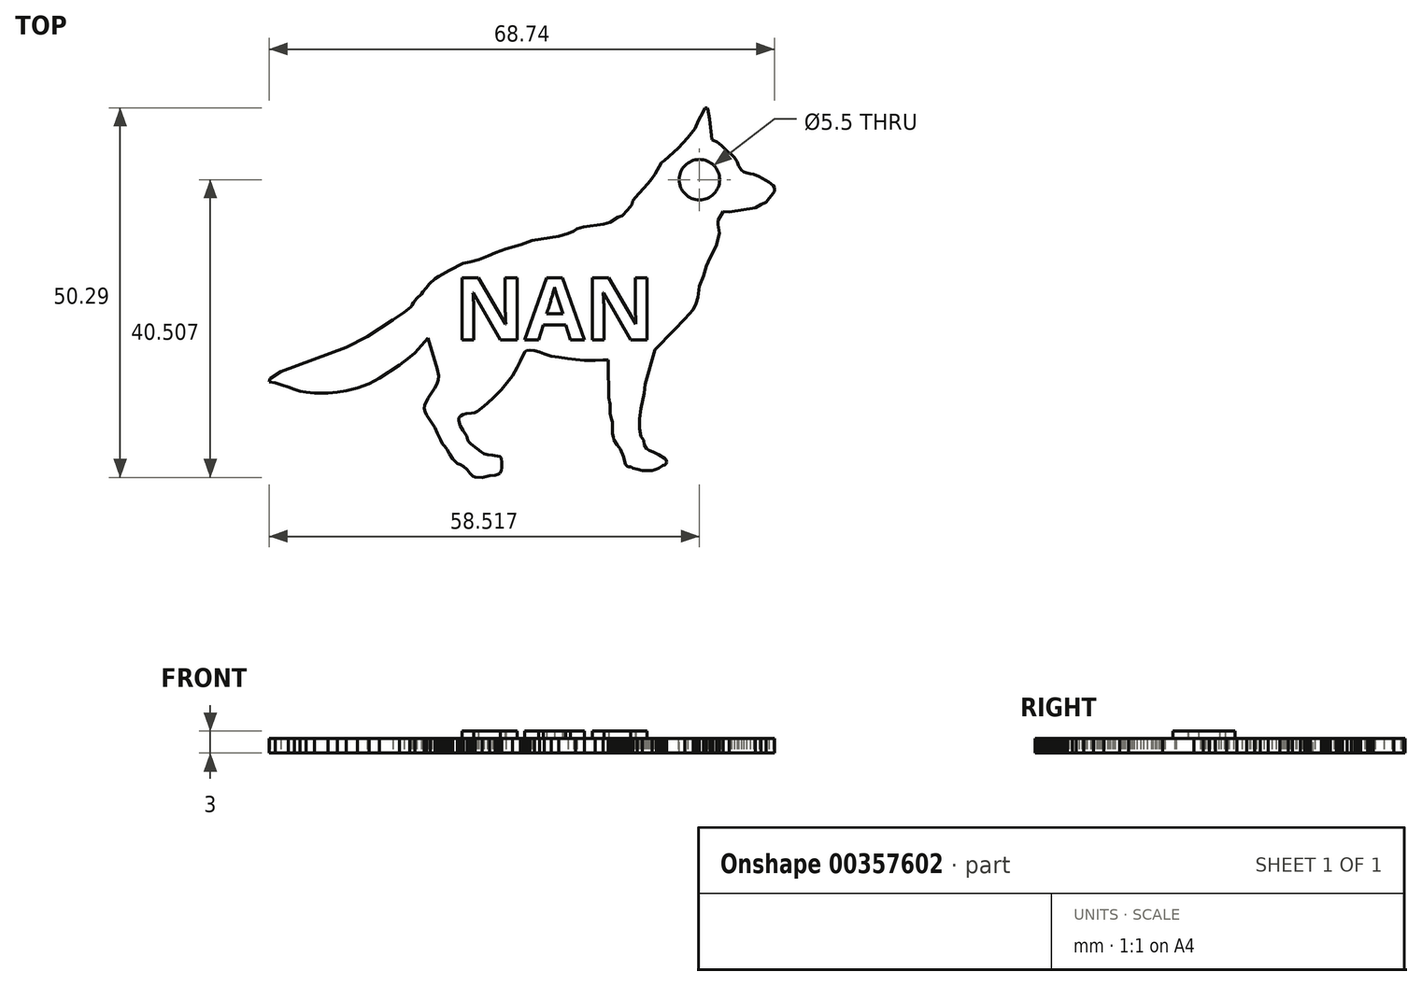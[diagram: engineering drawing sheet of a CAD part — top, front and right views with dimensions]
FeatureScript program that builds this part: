
annotation { "Feature Type Name" : "Feature", "Feature Type Description" : "" }
export const myFeature = defineFeature(function(context is Context, id is Id, definition is map)
    precondition{}
    {
        {
            var Q0;
            Q0=qCreatedBy(makeId("Top.planeOp"),FACE);
            var sketch = newSketch(context, id + "F0", { "sketchPlane" : qUnion([Q0])});
            skLineSegment(sketch, "E0", {"start": v(-14.95, 2.9) * mm, "end": v(-15.77, 3.38) * mm});
            skLineSegment(sketch, "E1", {"start": v(-15.77, 3.38) * mm, "end": v(-16.53, 3.78) * mm});
            skLineSegment(sketch, "E2", {"start": v(-16.53, 3.78) * mm, "end": v(-17.02, 3.97) * mm});
            skLineSegment(sketch, "E3", {"start": v(-17.02, 3.97) * mm, "end": v(-17.43, 4.22) * mm});
            skLineSegment(sketch, "E4", {"start": v(-17.43, 4.22) * mm, "end": v(-17.7, 4.7) * mm});
            skLineSegment(sketch, "E5", {"start": v(-17.7, 4.7) * mm, "end": v(-17.81, 5.35) * mm});
            skLineSegment(sketch, "E6", {"start": v(-17.81, 5.35) * mm, "end": v(-18.15, 5.86) * mm});
            skLineSegment(sketch, "E7", {"start": v(-18.15, 5.86) * mm, "end": v(-18.38, 6.92) * mm});
            skLineSegment(sketch, "E8", {"start": v(-18.38, 6.92) * mm, "end": v(-18.38, 8.25) * mm});
            skLineSegment(sketch, "E9", {"start": v(-18.38, 8.25) * mm, "end": v(-18.15, 9.65) * mm});
            skLineSegment(sketch, "E10", {"start": v(-18.15, 9.65) * mm, "end": v(-17.73, 11.8) * mm});
            skLineSegment(sketch, "E11", {"start": v(-17.73, 11.8) * mm, "end": v(-17.59, 12.98) * mm});
            skLineSegment(sketch, "E12", {"start": v(-17.59, 12.98) * mm, "end": v(-16.27, 17.65) * mm});
            skLineSegment(sketch, "E13", {"start": v(-16.27, 17.65) * mm, "end": v(-13.66, 20.33) * mm});
            skLineSegment(sketch, "E14", {"start": v(-13.66, 20.33) * mm, "end": v(-12.2, 21.87) * mm});
            skLineSegment(sketch, "E15", {"start": v(-12.2, 21.87) * mm, "end": v(-11.03, 23.13) * mm});
            skLineSegment(sketch, "E16", {"start": v(-11.03, 23.13) * mm, "end": v(-10.68, 23.98) * mm});
            skLineSegment(sketch, "E17", {"start": v(-10.68, 23.98) * mm, "end": v(-10.4, 24.8) * mm});
            skLineSegment(sketch, "E18", {"start": v(-10.4, 24.8) * mm, "end": v(-10.22, 26.33) * mm});
            skLineSegment(sketch, "E19", {"start": v(-10.22, 26.33) * mm, "end": v(-9.66, 27.72) * mm});
            skLineSegment(sketch, "E20", {"start": v(-9.66, 27.72) * mm, "end": v(-9.26, 29.04) * mm});
            skLineSegment(sketch, "E21", {"start": v(-9.26, 29.04) * mm, "end": v(-8.8, 30.16) * mm});
            skLineSegment(sketch, "E22", {"start": v(-8.8, 30.16) * mm, "end": v(-8.37, 30.9) * mm});
            skLineSegment(sketch, "E23", {"start": v(-8.37, 30.9) * mm, "end": v(-7.9, 31.98) * mm});
            skLineSegment(sketch, "E24", {"start": v(-7.9, 31.98) * mm, "end": v(-7.53, 33.57) * mm});
            skLineSegment(sketch, "E25", {"start": v(-7.53, 33.57) * mm, "end": v(-7.7, 34.7) * mm});
            skLineSegment(sketch, "E26", {"start": v(-7.7, 34.7) * mm, "end": v(-7.7, 35.26) * mm});
            skLineSegment(sketch, "E27", {"start": v(-7.7, 35.26) * mm, "end": v(-7, 36.5) * mm});
            skLineSegment(sketch, "E28", {"start": v(-7, 36.5) * mm, "end": v(-6.16, 36.4) * mm});
            skLineSegment(sketch, "E29", {"start": v(-6.16, 36.4) * mm, "end": v(-4.4, 36.68) * mm});
            skLineSegment(sketch, "E30", {"start": v(-4.4, 36.68) * mm, "end": v(-2.64, 36.96) * mm});
            skLineSegment(sketch, "E31", {"start": v(-2.64, 36.96) * mm, "end": v(-1.86, 37.41) * mm});
            skLineSegment(sketch, "E32", {"start": v(-1.86, 37.41) * mm, "end": v(-1.15, 37.72) * mm});
            skLineSegment(sketch, "E33", {"start": v(-1.15, 37.72) * mm, "end": v(0, 39.23) * mm});
            skLineSegment(sketch, "E34", {"start": v(0, 39.23) * mm, "end": v(0, 39.7) * mm});
            skLineSegment(sketch, "E35", {"start": v(0, 39.7) * mm, "end": v(-0.19, 40.04) * mm});
            skLineSegment(sketch, "E36", {"start": v(-0.19, 40.04) * mm, "end": v(-0.76, 40.45) * mm});
            skLineSegment(sketch, "E37", {"start": v(-0.76, 40.45) * mm, "end": v(-1.46, 40.85) * mm});
            skLineSegment(sketch, "E38", {"start": v(-1.46, 40.85) * mm, "end": v(-2.12, 41.23) * mm});
            skLineSegment(sketch, "E39", {"start": v(-2.12, 41.23) * mm, "end": v(-2.87, 41.52) * mm});
            skLineSegment(sketch, "E40", {"start": v(-2.87, 41.52) * mm, "end": v(-3.3, 41.64) * mm});
            skLineSegment(sketch, "E41", {"start": v(-3.3, 41.64) * mm, "end": v(-3.84, 41.73) * mm});
            skLineSegment(sketch, "E42", {"start": v(-3.84, 41.73) * mm, "end": v(-4.2, 41.84) * mm});
            skLineSegment(sketch, "E43", {"start": v(-4.2, 41.84) * mm, "end": v(-4.5, 42.1) * mm});
            skLineSegment(sketch, "E44", {"start": v(-4.5, 42.1) * mm, "end": v(-4.9, 42.72) * mm});
            skLineSegment(sketch, "E45", {"start": v(-4.9, 42.72) * mm, "end": v(-5.1, 43.29) * mm});
            skLineSegment(sketch, "E46", {"start": v(-5.1, 43.29) * mm, "end": v(-5.45, 43.82) * mm});
            skLineSegment(sketch, "E47", {"start": v(-5.45, 43.82) * mm, "end": v(-5.85, 44.2) * mm});
            skLineSegment(sketch, "E48", {"start": v(-5.85, 44.2) * mm, "end": v(-6.3, 44.53) * mm});
            skLineSegment(sketch, "E49", {"start": v(-6.3, 44.53) * mm, "end": v(-6.68, 44.91) * mm});
            skLineSegment(sketch, "E50", {"start": v(-6.68, 44.91) * mm, "end": v(-7.25, 45.5) * mm});
            skLineSegment(sketch, "E51", {"start": v(-7.25, 45.5) * mm, "end": v(-7.83, 45.96) * mm});
            skLineSegment(sketch, "E52", {"start": v(-7.83, 45.96) * mm, "end": v(-8.37, 46.17) * mm});
            skLineSegment(sketch, "E53", {"start": v(-8.37, 46.17) * mm, "end": v(-8.54, 46.27) * mm});
            skLineSegment(sketch, "E54", {"start": v(-8.54, 46.27) * mm, "end": v(-8.7, 47.7) * mm});
            skLineSegment(sketch, "E55", {"start": v(-8.7, 47.7) * mm, "end": v(-8.85, 49.08) * mm});
            skLineSegment(sketch, "E56", {"start": v(-8.85, 49.08) * mm, "end": v(-8.98, 49.9) * mm});
            skLineSegment(sketch, "E57", {"start": v(-8.98, 49.9) * mm, "end": v(-9.07, 50.42) * mm});
            skLineSegment(sketch, "E58", {"start": v(-9.07, 50.42) * mm, "end": v(-9.18, 50.6) * mm});
            skLineSegment(sketch, "E59", {"start": v(-9.18, 50.6) * mm, "end": v(-9.49, 50.6) * mm});
            skLineSegment(sketch, "E60", {"start": v(-9.49, 50.6) * mm, "end": v(-9.72, 50) * mm});
            skLineSegment(sketch, "E61", {"start": v(-9.72, 50) * mm, "end": v(-10.4, 48.84) * mm});
            skLineSegment(sketch, "E62", {"start": v(-10.4, 48.84) * mm, "end": v(-10.82, 47.75) * mm});
            skLineSegment(sketch, "E63", {"start": v(-10.82, 47.75) * mm, "end": v(-11.83, 46.54) * mm});
            skLineSegment(sketch, "E64", {"start": v(-11.83, 46.54) * mm, "end": v(-13.12, 45.13) * mm});
            skLineSegment(sketch, "E65", {"start": v(-13.12, 45.13) * mm, "end": v(-14.32, 44.02) * mm});
            skLineSegment(sketch, "E66", {"start": v(-14.32, 44.02) * mm, "end": v(-14.98, 43.42) * mm});
            skLineSegment(sketch, "E67", {"start": v(-14.98, 43.42) * mm, "end": v(-15.37, 43.16) * mm});
            skLineSegment(sketch, "E68", {"start": v(-15.37, 43.16) * mm, "end": v(-15.71, 42.57) * mm});
            skLineSegment(sketch, "E69", {"start": v(-15.71, 42.57) * mm, "end": v(-16, 42.06) * mm});
            skLineSegment(sketch, "E70", {"start": v(-16, 42.06) * mm, "end": v(-16.28, 41.58) * mm});
            skLineSegment(sketch, "E71", {"start": v(-16.28, 41.58) * mm, "end": v(-16.73, 40.92) * mm});
            skLineSegment(sketch, "E72", {"start": v(-16.73, 40.92) * mm, "end": v(-17.23, 40.3) * mm});
            skLineSegment(sketch, "E73", {"start": v(-17.23, 40.3) * mm, "end": v(-17.66, 39.84) * mm});
            skLineSegment(sketch, "E74", {"start": v(-17.66, 39.84) * mm, "end": v(-18.32, 39.12) * mm});
            skLineSegment(sketch, "E75", {"start": v(-18.32, 39.12) * mm, "end": v(-19.03, 38.34) * mm});
            skLineSegment(sketch, "E76", {"start": v(-19.03, 38.34) * mm, "end": v(-19.31, 37.85) * mm});
            skLineSegment(sketch, "E77", {"start": v(-19.31, 37.85) * mm, "end": v(-19.36, 37.43) * mm});
            skLineSegment(sketch, "E78", {"start": v(-19.36, 37.43) * mm, "end": v(-20, 36.64) * mm});
            skLineSegment(sketch, "E79", {"start": v(-20, 36.64) * mm, "end": v(-20.7, 35.88) * mm});
            skLineSegment(sketch, "E80", {"start": v(-20.7, 35.88) * mm, "end": v(-21.28, 35.72) * mm});
            skLineSegment(sketch, "E81", {"start": v(-21.28, 35.72) * mm, "end": v(-21.99, 35.26) * mm});
            skLineSegment(sketch, "E82", {"start": v(-21.99, 35.26) * mm, "end": v(-22.36, 35.02) * mm});
            skLineSegment(sketch, "E83", {"start": v(-22.36, 35.02) * mm, "end": v(-23.28, 34.77) * mm});
            skLineSegment(sketch, "E84", {"start": v(-23.28, 34.77) * mm, "end": v(-24.64, 34.56) * mm});
            skLineSegment(sketch, "E85", {"start": v(-24.64, 34.56) * mm, "end": v(-25.96, 34.35) * mm});
            skLineSegment(sketch, "E86", {"start": v(-25.96, 34.35) * mm, "end": v(-26.87, 34.1) * mm});
            skLineSegment(sketch, "E87", {"start": v(-26.87, 34.1) * mm, "end": v(-27.33, 33.8) * mm});
            skLineSegment(sketch, "E88", {"start": v(-27.33, 33.8) * mm, "end": v(-28.05, 33.46) * mm});
            skLineSegment(sketch, "E89", {"start": v(-28.05, 33.46) * mm, "end": v(-29.37, 33.1) * mm});
            skLineSegment(sketch, "E90", {"start": v(-29.37, 33.1) * mm, "end": v(-33, 32.52) * mm});
            skLineSegment(sketch, "E91", {"start": v(-33, 32.52) * mm, "end": v(-34.5, 31.95) * mm});
            skLineSegment(sketch, "E92", {"start": v(-34.5, 31.95) * mm, "end": v(-35.33, 31.72) * mm});
            skLineSegment(sketch, "E93", {"start": v(-35.33, 31.72) * mm, "end": v(-36.54, 31.39) * mm});
            skLineSegment(sketch, "E94", {"start": v(-36.54, 31.39) * mm, "end": v(-37.9, 30.86) * mm});
            skLineSegment(sketch, "E95", {"start": v(-37.9, 30.86) * mm, "end": v(-38.91, 30.41) * mm});
            skLineSegment(sketch, "E96", {"start": v(-38.91, 30.41) * mm, "end": v(-40.2, 29.93) * mm});
            skLineSegment(sketch, "E97", {"start": v(-40.2, 29.93) * mm, "end": v(-41.45, 29.6) * mm});
            skLineSegment(sketch, "E98", {"start": v(-41.45, 29.6) * mm, "end": v(-42.34, 29.45) * mm});
            skLineSegment(sketch, "E99", {"start": v(-42.34, 29.45) * mm, "end": v(-44.21, 28.45) * mm});
            skLineSegment(sketch, "E100", {"start": v(-44.21, 28.45) * mm, "end": v(-45.68, 27.64) * mm});
            skLineSegment(sketch, "E101", {"start": v(-45.68, 27.64) * mm, "end": v(-46.17, 27.32) * mm});
            skLineSegment(sketch, "E102", {"start": v(-46.17, 27.32) * mm, "end": v(-46.92, 26.63) * mm});
            skLineSegment(sketch, "E103", {"start": v(-46.92, 26.63) * mm, "end": v(-47.4, 26.04) * mm});
            skLineSegment(sketch, "E104", {"start": v(-47.4, 26.04) * mm, "end": v(-47.83, 25.56) * mm});
            skLineSegment(sketch, "E105", {"start": v(-47.83, 25.56) * mm, "end": v(-48, 25.25) * mm});
            skLineSegment(sketch, "E106", {"start": v(-48, 25.25) * mm, "end": v(-48.68, 24.63) * mm});
            skLineSegment(sketch, "E107", {"start": v(-48.68, 24.63) * mm, "end": v(-49.1, 24.1) * mm});
            skLineSegment(sketch, "E108", {"start": v(-49.1, 24.1) * mm, "end": v(-49.3, 23.77) * mm});
            skLineSegment(sketch, "E109", {"start": v(-49.3, 23.77) * mm, "end": v(-49.4, 23.49) * mm});
            skLineSegment(sketch, "E110", {"start": v(-49.4, 23.49) * mm, "end": v(-50.38, 22.77) * mm});
            skLineSegment(sketch, "E111", {"start": v(-50.38, 22.77) * mm, "end": v(-51.87, 21.74) * mm});
            skLineSegment(sketch, "E112", {"start": v(-51.87, 21.74) * mm, "end": v(-53.68, 20.56) * mm});
            skLineSegment(sketch, "E113", {"start": v(-53.68, 20.56) * mm, "end": v(-55.36, 19.48) * mm});
            skLineSegment(sketch, "E114", {"start": v(-55.36, 19.48) * mm, "end": v(-58.23, 17.97) * mm});
            skLineSegment(sketch, "E115", {"start": v(-58.23, 17.97) * mm, "end": v(-61, 16.94) * mm});
            skLineSegment(sketch, "E116", {"start": v(-61, 16.94) * mm, "end": v(-63.15, 16.14) * mm});
            skLineSegment(sketch, "E117", {"start": v(-63.15, 16.14) * mm, "end": v(-65.63, 15.22) * mm});
            skLineSegment(sketch, "E118", {"start": v(-65.63, 15.22) * mm, "end": v(-67.14, 14.66) * mm});
            skLineSegment(sketch, "E119", {"start": v(-67.14, 14.66) * mm, "end": v(-68, 14.1) * mm});
            skLineSegment(sketch, "E120", {"start": v(-68, 14.1) * mm, "end": v(-68.58, 13.73) * mm});
            skLineSegment(sketch, "E121", {"start": v(-68.58, 13.73) * mm, "end": v(-68.74, 13.32) * mm});
            skLineSegment(sketch, "E122", {"start": v(-68.74, 13.32) * mm, "end": v(-67.9, 13.15) * mm});
            skLineSegment(sketch, "E123", {"start": v(-67.9, 13.15) * mm, "end": v(-66.97, 12.84) * mm});
            skLineSegment(sketch, "E124", {"start": v(-66.97, 12.84) * mm, "end": v(-66.14, 12.58) * mm});
            skLineSegment(sketch, "E125", {"start": v(-66.14, 12.58) * mm, "end": v(-65.31, 12.25) * mm});
            skLineSegment(sketch, "E126", {"start": v(-65.31, 12.25) * mm, "end": v(-64.52, 12.02) * mm});
            skLineSegment(sketch, "E127", {"start": v(-64.52, 12.02) * mm, "end": v(-63.68, 11.92) * mm});
            skLineSegment(sketch, "E128", {"start": v(-63.68, 11.92) * mm, "end": v(-62.6, 11.8) * mm});
            skLineSegment(sketch, "E129", {"start": v(-62.6, 11.8) * mm, "end": v(-60.73, 11.8) * mm});
            skLineSegment(sketch, "E130", {"start": v(-60.73, 11.8) * mm, "end": v(-59.44, 11.88) * mm});
            skLineSegment(sketch, "E131", {"start": v(-59.44, 11.88) * mm, "end": v(-58.22, 12.07) * mm});
            skLineSegment(sketch, "E132", {"start": v(-58.22, 12.07) * mm, "end": v(-56.72, 12.48) * mm});
            skLineSegment(sketch, "E133", {"start": v(-56.72, 12.48) * mm, "end": v(-55.15, 13.06) * mm});
            skLineSegment(sketch, "E134", {"start": v(-55.15, 13.06) * mm, "end": v(-53.74, 13.78) * mm});
            skLineSegment(sketch, "E135", {"start": v(-53.74, 13.78) * mm, "end": v(-52.55, 14.56) * mm});
            skLineSegment(sketch, "E136", {"start": v(-52.55, 14.56) * mm, "end": v(-51, 15.56) * mm});
            skLineSegment(sketch, "E137", {"start": v(-51, 15.56) * mm, "end": v(-49.58, 16.64) * mm});
            skLineSegment(sketch, "E138", {"start": v(-49.58, 16.64) * mm, "end": v(-48.94, 17.2) * mm});
            skLineSegment(sketch, "E139", {"start": v(-48.94, 17.2) * mm, "end": v(-47.13, 19.27) * mm});
            skLineSegment(sketch, "E140", {"start": v(-47.13, 19.27) * mm, "end": v(-46.18, 16.12) * mm});
            skLineSegment(sketch, "E141", {"start": v(-46.18, 16.12) * mm, "end": v(-45.84, 15.01) * mm});
            skLineSegment(sketch, "E142", {"start": v(-45.84, 15.01) * mm, "end": v(-45.69, 14.15) * mm});
            skLineSegment(sketch, "E143", {"start": v(-45.69, 14.15) * mm, "end": v(-45.73, 13.58) * mm});
            skLineSegment(sketch, "E144", {"start": v(-45.73, 13.58) * mm, "end": v(-45.9, 12.97) * mm});
            skLineSegment(sketch, "E145", {"start": v(-45.9, 12.97) * mm, "end": v(-46.23, 12.4) * mm});
            skLineSegment(sketch, "E146", {"start": v(-46.23, 12.4) * mm, "end": v(-46.63, 11.84) * mm});
            skLineSegment(sketch, "E147", {"start": v(-46.63, 11.84) * mm, "end": v(-47.15, 11.08) * mm});
            skLineSegment(sketch, "E148", {"start": v(-47.15, 11.08) * mm, "end": v(-47.6, 10.14) * mm});
            skLineSegment(sketch, "E149", {"start": v(-47.6, 10.14) * mm, "end": v(-47.63, 9.65) * mm});
            skLineSegment(sketch, "E150", {"start": v(-47.63, 9.65) * mm, "end": v(-47.54, 9.2) * mm});
            skLineSegment(sketch, "E151", {"start": v(-47.54, 9.2) * mm, "end": v(-47.33, 8.8) * mm});
            skLineSegment(sketch, "E152", {"start": v(-47.33, 8.8) * mm, "end": v(-46.82, 8.01) * mm});
            skLineSegment(sketch, "E153", {"start": v(-46.82, 8.01) * mm, "end": v(-46.18, 7.06) * mm});
            skLineSegment(sketch, "E154", {"start": v(-46.18, 7.06) * mm, "end": v(-45.86, 6.3) * mm});
            skLineSegment(sketch, "E155", {"start": v(-45.86, 6.3) * mm, "end": v(-45.43, 5.45) * mm});
            skLineSegment(sketch, "E156", {"start": v(-45.43, 5.45) * mm, "end": v(-45.16, 4.88) * mm});
            skLineSegment(sketch, "E157", {"start": v(-45.16, 4.88) * mm, "end": v(-44.86, 4.52) * mm});
            skLineSegment(sketch, "E158", {"start": v(-44.86, 4.52) * mm, "end": v(-44.53, 4.06) * mm});
            skLineSegment(sketch, "E159", {"start": v(-44.53, 4.06) * mm, "end": v(-44.2, 3.5) * mm});
            skLineSegment(sketch, "E160", {"start": v(-44.2, 3.5) * mm, "end": v(-43.76, 2.83) * mm});
            skLineSegment(sketch, "E161", {"start": v(-43.76, 2.83) * mm, "end": v(-43.14, 2.17) * mm});
            skLineSegment(sketch, "E162", {"start": v(-43.14, 2.17) * mm, "end": v(-42.73, 2.09) * mm});
            skLineSegment(sketch, "E163", {"start": v(-42.73, 2.09) * mm, "end": v(-42.3, 1.8) * mm});
            skLineSegment(sketch, "E164", {"start": v(-42.3, 1.8) * mm, "end": v(-41.8, 1.37) * mm});
            skLineSegment(sketch, "E165", {"start": v(-41.8, 1.37) * mm, "end": v(-41.44, 0.88) * mm});
            skLineSegment(sketch, "E166", {"start": v(-41.44, 0.88) * mm, "end": v(-41.02, 0.5) * mm});
            skLineSegment(sketch, "E167", {"start": v(-41.02, 0.5) * mm, "end": v(-40.75, 0.35) * mm});
            skLineSegment(sketch, "E168", {"start": v(-40.75, 0.35) * mm, "end": v(-39.74, 0.3) * mm});
            skLineSegment(sketch, "E169", {"start": v(-39.74, 0.3) * mm, "end": v(-38.76, 0.5) * mm});
            skLineSegment(sketch, "E170", {"start": v(-38.76, 0.5) * mm, "end": v(-37.96, 0.6) * mm});
            skLineSegment(sketch, "E171", {"start": v(-37.96, 0.6) * mm, "end": v(-37.63, 0.7) * mm});
            skLineSegment(sketch, "E172", {"start": v(-37.63, 0.7) * mm, "end": v(-37.35, 0.87) * mm});
            skLineSegment(sketch, "E173", {"start": v(-37.35, 0.87) * mm, "end": v(-37.16, 1.2) * mm});
            skLineSegment(sketch, "E174", {"start": v(-37.16, 1.2) * mm, "end": v(-37.08, 1.6) * mm});
            skLineSegment(sketch, "E175", {"start": v(-37.08, 1.6) * mm, "end": v(-37.08, 2.3) * mm});
            skLineSegment(sketch, "E176", {"start": v(-37.08, 2.3) * mm, "end": v(-37.17, 2.95) * mm});
            skLineSegment(sketch, "E177", {"start": v(-37.17, 2.95) * mm, "end": v(-37.34, 3.14) * mm});
            skLineSegment(sketch, "E178", {"start": v(-37.34, 3.14) * mm, "end": v(-37.74, 3.22) * mm});
            skLineSegment(sketch, "E179", {"start": v(-37.74, 3.22) * mm, "end": v(-38.35, 3.35) * mm});
            skLineSegment(sketch, "E180", {"start": v(-38.35, 3.35) * mm, "end": v(-38.99, 3.4) * mm});
            skLineSegment(sketch, "E181", {"start": v(-38.99, 3.4) * mm, "end": v(-39.5, 3.5) * mm});
            skLineSegment(sketch, "E182", {"start": v(-39.5, 3.5) * mm, "end": v(-39.92, 3.76) * mm});
            skLineSegment(sketch, "E183", {"start": v(-39.92, 3.76) * mm, "end": v(-40.48, 4.21) * mm});
            skLineSegment(sketch, "E184", {"start": v(-40.48, 4.21) * mm, "end": v(-41.3, 4.84) * mm});
            skLineSegment(sketch, "E185", {"start": v(-41.3, 4.84) * mm, "end": v(-41.6, 5.17) * mm});
            skLineSegment(sketch, "E186", {"start": v(-41.6, 5.17) * mm, "end": v(-41.73, 5.45) * mm});
            skLineSegment(sketch, "E187", {"start": v(-41.73, 5.45) * mm, "end": v(-41.87, 5.93) * mm});
            skLineSegment(sketch, "E188", {"start": v(-41.87, 5.93) * mm, "end": v(-42.36, 6.68) * mm});
            skLineSegment(sketch, "E189", {"start": v(-42.36, 6.68) * mm, "end": v(-42.76, 7.34) * mm});
            skLineSegment(sketch, "E190", {"start": v(-42.76, 7.34) * mm, "end": v(-42.96, 8.01) * mm});
            skLineSegment(sketch, "E191", {"start": v(-42.96, 8.01) * mm, "end": v(-42.96, 8.38) * mm});
            skLineSegment(sketch, "E192", {"start": v(-42.96, 8.38) * mm, "end": v(-42.7, 8.65) * mm});
            skLineSegment(sketch, "E193", {"start": v(-42.7, 8.65) * mm, "end": v(-42.35, 8.86) * mm});
            skLineSegment(sketch, "E194", {"start": v(-42.35, 8.86) * mm, "end": v(-41.9, 8.96) * mm});
            skLineSegment(sketch, "E195", {"start": v(-41.9, 8.96) * mm, "end": v(-41.2, 9.02) * mm});
            skLineSegment(sketch, "E196", {"start": v(-41.2, 9.02) * mm, "end": v(-40.81, 9.1) * mm});
            skLineSegment(sketch, "E197", {"start": v(-40.81, 9.1) * mm, "end": v(-40.41, 9.27) * mm});
            skLineSegment(sketch, "E198", {"start": v(-40.41, 9.27) * mm, "end": v(-39.84, 9.76) * mm});
            skLineSegment(sketch, "E199", {"start": v(-39.84, 9.76) * mm, "end": v(-39.04, 10.4) * mm});
            skLineSegment(sketch, "E200", {"start": v(-39.04, 10.4) * mm, "end": v(-38.2, 11.17) * mm});
            skLineSegment(sketch, "E201", {"start": v(-38.2, 11.17) * mm, "end": v(-37.15, 12.2) * mm});
            skLineSegment(sketch, "E202", {"start": v(-37.15, 12.2) * mm, "end": v(-36.4, 13.15) * mm});
            skLineSegment(sketch, "E203", {"start": v(-36.4, 13.15) * mm, "end": v(-35.6, 14.15) * mm});
            skLineSegment(sketch, "E204", {"start": v(-35.6, 14.15) * mm, "end": v(-35, 15.28) * mm});
            skLineSegment(sketch, "E205", {"start": v(-35, 15.28) * mm, "end": v(-34.55, 16.12) * mm});
            skLineSegment(sketch, "E206", {"start": v(-34.55, 16.12) * mm, "end": v(-34.24, 16.82) * mm});
            skLineSegment(sketch, "E207", {"start": v(-34.24, 16.82) * mm, "end": v(-33.95, 17.43) * mm});
            skLineSegment(sketch, "E208", {"start": v(-33.95, 17.43) * mm, "end": v(-33.71, 17.52) * mm});
            skLineSegment(sketch, "E209", {"start": v(-33.71, 17.52) * mm, "end": v(-33.3, 17.59) * mm});
            skLineSegment(sketch, "E210", {"start": v(-33.3, 17.59) * mm, "end": v(-32.65, 17.53) * mm});
            skLineSegment(sketch, "E211", {"start": v(-32.65, 17.53) * mm, "end": v(-31.95, 17.39) * mm});
            skLineSegment(sketch, "E212", {"start": v(-31.95, 17.39) * mm, "end": v(-31.33, 17.1) * mm});
            skLineSegment(sketch, "E213", {"start": v(-31.33, 17.1) * mm, "end": v(-30.35, 16.81) * mm});
            skLineSegment(sketch, "E214", {"start": v(-30.35, 16.81) * mm, "end": v(-29.36, 16.64) * mm});
            skLineSegment(sketch, "E215", {"start": v(-29.36, 16.64) * mm, "end": v(-28.16, 16.48) * mm});
            skLineSegment(sketch, "E216", {"start": v(-28.16, 16.48) * mm, "end": v(-27.05, 16.33) * mm});
            skLineSegment(sketch, "E217", {"start": v(-27.05, 16.33) * mm, "end": v(-25.85, 16.22) * mm});
            skLineSegment(sketch, "E218", {"start": v(-25.85, 16.22) * mm, "end": v(-24.4, 16.22) * mm});
            skLineSegment(sketch, "E219", {"start": v(-24.4, 16.22) * mm, "end": v(-23.3, 16.25) * mm});
            skLineSegment(sketch, "E220", {"start": v(-23.3, 16.25) * mm, "end": v(-22.65, 16.25) * mm});
            skLineSegment(sketch, "E221", {"start": v(-22.65, 16.25) * mm, "end": v(-22.65, 14.95) * mm});
            skLineSegment(sketch, "E222", {"start": v(-22.65, 14.95) * mm, "end": v(-22.65, 13.65) * mm});
            skLineSegment(sketch, "E223", {"start": v(-22.65, 13.65) * mm, "end": v(-22.58, 13.3) * mm});
            skLineSegment(sketch, "E224", {"start": v(-22.58, 13.3) * mm, "end": v(-22.54, 11.17) * mm});
            skLineSegment(sketch, "E225", {"start": v(-22.54, 11.17) * mm, "end": v(-22.49, 10.87) * mm});
            skLineSegment(sketch, "E226", {"start": v(-22.49, 10.87) * mm, "end": v(-22.41, 10.52) * mm});
            skLineSegment(sketch, "E227", {"start": v(-22.41, 10.52) * mm, "end": v(-22.35, 10.3) * mm});
            skLineSegment(sketch, "E228", {"start": v(-22.35, 10.3) * mm, "end": v(-22.35, 8.98) * mm});
            skLineSegment(sketch, "E229", {"start": v(-22.35, 8.98) * mm, "end": v(-22.28, 8.66) * mm});
            skLineSegment(sketch, "E230", {"start": v(-22.28, 8.66) * mm, "end": v(-22.19, 8.22) * mm});
            skLineSegment(sketch, "E231", {"start": v(-22.19, 8.22) * mm, "end": v(-22.03, 7.85) * mm});
            skLineSegment(sketch, "E232", {"start": v(-22.03, 7.85) * mm, "end": v(-22.03, 6.25) * mm});
            skLineSegment(sketch, "E233", {"start": v(-22.03, 6.25) * mm, "end": v(-21.93, 5.8) * mm});
            skLineSegment(sketch, "E234", {"start": v(-21.93, 5.8) * mm, "end": v(-21.83, 5.45) * mm});
            skLineSegment(sketch, "E235", {"start": v(-21.83, 5.45) * mm, "end": v(-21.64, 5.13) * mm});
            skLineSegment(sketch, "E236", {"start": v(-21.64, 5.13) * mm, "end": v(-21.4, 4.75) * mm});
            skLineSegment(sketch, "E237", {"start": v(-21.4, 4.75) * mm, "end": v(-21.17, 4.39) * mm});
            skLineSegment(sketch, "E238", {"start": v(-21.17, 4.39) * mm, "end": v(-21, 4.16) * mm});
            skLineSegment(sketch, "E239", {"start": v(-21, 4.16) * mm, "end": v(-20.72, 3.5) * mm});
            skLineSegment(sketch, "E240", {"start": v(-20.72, 3.5) * mm, "end": v(-20.52, 3.04) * mm});
            skLineSegment(sketch, "E241", {"start": v(-20.52, 3.04) * mm, "end": v(-20.41, 2.5) * mm});
            skLineSegment(sketch, "E242", {"start": v(-20.41, 2.5) * mm, "end": v(-20.27, 2.04) * mm});
            skLineSegment(sketch, "E243", {"start": v(-20.27, 2.04) * mm, "end": v(-20.04, 1.82) * mm});
            skLineSegment(sketch, "E244", {"start": v(-20.04, 1.82) * mm, "end": v(-19.85, 1.74) * mm});
            skLineSegment(sketch, "E245", {"start": v(-19.85, 1.74) * mm, "end": v(-19.52, 1.71) * mm});
            skLineSegment(sketch, "E246", {"start": v(-19.52, 1.71) * mm, "end": v(-19.23, 1.56) * mm});
            skLineSegment(sketch, "E247", {"start": v(-19.23, 1.56) * mm, "end": v(-18.68, 1.4) * mm});
            skLineSegment(sketch, "E248", {"start": v(-18.68, 1.4) * mm, "end": v(-17.98, 1.25) * mm});
            skLineSegment(sketch, "E249", {"start": v(-17.98, 1.25) * mm, "end": v(-16.65, 1.25) * mm});
            skLineSegment(sketch, "E250", {"start": v(-16.65, 1.25) * mm, "end": v(-16.1, 1.42) * mm});
            skLineSegment(sketch, "E251", {"start": v(-16.1, 1.42) * mm, "end": v(-15.73, 1.57) * mm});
            skLineSegment(sketch, "E252", {"start": v(-15.73, 1.57) * mm, "end": v(-15.4, 1.77) * mm});
            skLineSegment(sketch, "E253", {"start": v(-15.4, 1.77) * mm, "end": v(-15.17, 1.95) * mm});
            skLineSegment(sketch, "E254", {"start": v(-15.17, 1.95) * mm, "end": v(-14.93, 2) * mm});
            skLineSegment(sketch, "E255", {"start": v(-14.93, 2) * mm, "end": v(-14.75, 2.2) * mm});
            skLineSegment(sketch, "E256", {"start": v(-14.75, 2.2) * mm, "end": v(-14.7, 2.4) * mm});
            skLineSegment(sketch, "E257", {"start": v(-14.7, 2.4) * mm, "end": v(-14.76, 2.66) * mm});
            skLineSegment(sketch, "E258", {"start": v(-14.76, 2.66) * mm, "end": v(-14.95, 2.9) * mm});
            skSolve(sketch);
        }
        {
            var Q0;
            Q0 = qSketchRegion(id + "F0", true);
            extrude(context, id + "F1", {"entities" : qUnion([Q0]), "depth" : 2 * mm});
        }
        {
            var Q0;
            Q0=makeQuery(id+"F1.opExtrude","CAP_FACE",FACE,{"disambiguationData":[OSD([sQuery(id+"F0.wireOp",EDGE,"E0"),sQuery(id+"F0.wireOp",EDGE,"E1"),sQuery(id+"F0.wireOp",EDGE,"E2"),sQuery(id+"F0.wireOp",EDGE,"E3"),sQuery(id+"F0.wireOp",EDGE,"E4"),sQuery(id+"F0.wireOp",EDGE,"E5"),sQuery(id+"F0.wireOp",EDGE,"E6"),sQuery(id+"F0.wireOp",EDGE,"E7"),sQuery(id+"F0.wireOp",EDGE,"E8"),sQuery(id+"F0.wireOp",EDGE,"E9"),sQuery(id+"F0.wireOp",EDGE,"E10"),sQuery(id+"F0.wireOp",EDGE,"E11"),sQuery(id+"F0.wireOp",EDGE,"E12"),sQuery(id+"F0.wireOp",EDGE,"E13"),sQuery(id+"F0.wireOp",EDGE,"E14"),sQuery(id+"F0.wireOp",EDGE,"E15"),sQuery(id+"F0.wireOp",EDGE,"E16"),sQuery(id+"F0.wireOp",EDGE,"E17"),sQuery(id+"F0.wireOp",EDGE,"E18"),sQuery(id+"F0.wireOp",EDGE,"E19"),sQuery(id+"F0.wireOp",EDGE,"E20"),sQuery(id+"F0.wireOp",EDGE,"E21"),sQuery(id+"F0.wireOp",EDGE,"E22"),sQuery(id+"F0.wireOp",EDGE,"E23"),sQuery(id+"F0.wireOp",EDGE,"E24"),sQuery(id+"F0.wireOp",EDGE,"E25"),sQuery(id+"F0.wireOp",EDGE,"E26"),sQuery(id+"F0.wireOp",EDGE,"E27"),sQuery(id+"F0.wireOp",EDGE,"E28"),sQuery(id+"F0.wireOp",EDGE,"E29"),sQuery(id+"F0.wireOp",EDGE,"E30"),sQuery(id+"F0.wireOp",EDGE,"E31"),sQuery(id+"F0.wireOp",EDGE,"E32"),sQuery(id+"F0.wireOp",EDGE,"E33"),sQuery(id+"F0.wireOp",EDGE,"E34"),sQuery(id+"F0.wireOp",EDGE,"E35"),sQuery(id+"F0.wireOp",EDGE,"E36"),sQuery(id+"F0.wireOp",EDGE,"E37"),sQuery(id+"F0.wireOp",EDGE,"E38"),sQuery(id+"F0.wireOp",EDGE,"E39"),sQuery(id+"F0.wireOp",EDGE,"E40"),sQuery(id+"F0.wireOp",EDGE,"E41"),sQuery(id+"F0.wireOp",EDGE,"E42"),sQuery(id+"F0.wireOp",EDGE,"E43"),sQuery(id+"F0.wireOp",EDGE,"E44"),sQuery(id+"F0.wireOp",EDGE,"E45"),sQuery(id+"F0.wireOp",EDGE,"E46"),sQuery(id+"F0.wireOp",EDGE,"E47"),sQuery(id+"F0.wireOp",EDGE,"E48"),sQuery(id+"F0.wireOp",EDGE,"E49"),sQuery(id+"F0.wireOp",EDGE,"E50"),sQuery(id+"F0.wireOp",EDGE,"E51"),sQuery(id+"F0.wireOp",EDGE,"E52"),sQuery(id+"F0.wireOp",EDGE,"E53"),sQuery(id+"F0.wireOp",EDGE,"E54"),sQuery(id+"F0.wireOp",EDGE,"E55"),sQuery(id+"F0.wireOp",EDGE,"E56"),sQuery(id+"F0.wireOp",EDGE,"E57"),sQuery(id+"F0.wireOp",EDGE,"E58"),sQuery(id+"F0.wireOp",EDGE,"E59"),sQuery(id+"F0.wireOp",EDGE,"E60"),sQuery(id+"F0.wireOp",EDGE,"E61"),sQuery(id+"F0.wireOp",EDGE,"E62"),sQuery(id+"F0.wireOp",EDGE,"E63"),sQuery(id+"F0.wireOp",EDGE,"E64"),sQuery(id+"F0.wireOp",EDGE,"E65"),sQuery(id+"F0.wireOp",EDGE,"E66"),sQuery(id+"F0.wireOp",EDGE,"E67"),sQuery(id+"F0.wireOp",EDGE,"E68"),sQuery(id+"F0.wireOp",EDGE,"E69"),sQuery(id+"F0.wireOp",EDGE,"E70"),sQuery(id+"F0.wireOp",EDGE,"E71"),sQuery(id+"F0.wireOp",EDGE,"E72"),sQuery(id+"F0.wireOp",EDGE,"E73"),sQuery(id+"F0.wireOp",EDGE,"E74"),sQuery(id+"F0.wireOp",EDGE,"E75"),sQuery(id+"F0.wireOp",EDGE,"E76"),sQuery(id+"F0.wireOp",EDGE,"E77"),sQuery(id+"F0.wireOp",EDGE,"E78"),sQuery(id+"F0.wireOp",EDGE,"E79"),sQuery(id+"F0.wireOp",EDGE,"E80"),sQuery(id+"F0.wireOp",EDGE,"E81"),sQuery(id+"F0.wireOp",EDGE,"E82"),sQuery(id+"F0.wireOp",EDGE,"E83"),sQuery(id+"F0.wireOp",EDGE,"E84"),sQuery(id+"F0.wireOp",EDGE,"E85"),sQuery(id+"F0.wireOp",EDGE,"E86"),sQuery(id+"F0.wireOp",EDGE,"E87"),sQuery(id+"F0.wireOp",EDGE,"E88"),sQuery(id+"F0.wireOp",EDGE,"E89"),sQuery(id+"F0.wireOp",EDGE,"E90"),sQuery(id+"F0.wireOp",EDGE,"E91"),sQuery(id+"F0.wireOp",EDGE,"E92"),sQuery(id+"F0.wireOp",EDGE,"E93"),sQuery(id+"F0.wireOp",EDGE,"E94"),sQuery(id+"F0.wireOp",EDGE,"E95"),sQuery(id+"F0.wireOp",EDGE,"E96"),sQuery(id+"F0.wireOp",EDGE,"E97"),sQuery(id+"F0.wireOp",EDGE,"E98"),sQuery(id+"F0.wireOp",EDGE,"E99"),sQuery(id+"F0.wireOp",EDGE,"E100"),sQuery(id+"F0.wireOp",EDGE,"E101"),sQuery(id+"F0.wireOp",EDGE,"E102"),sQuery(id+"F0.wireOp",EDGE,"E103"),sQuery(id+"F0.wireOp",EDGE,"E104"),sQuery(id+"F0.wireOp",EDGE,"E105"),sQuery(id+"F0.wireOp",EDGE,"E106"),sQuery(id+"F0.wireOp",EDGE,"E107"),sQuery(id+"F0.wireOp",EDGE,"E108"),sQuery(id+"F0.wireOp",EDGE,"E109"),sQuery(id+"F0.wireOp",EDGE,"E110"),sQuery(id+"F0.wireOp",EDGE,"E111"),sQuery(id+"F0.wireOp",EDGE,"E112"),sQuery(id+"F0.wireOp",EDGE,"E113"),sQuery(id+"F0.wireOp",EDGE,"E114"),sQuery(id+"F0.wireOp",EDGE,"E115"),sQuery(id+"F0.wireOp",EDGE,"E116"),sQuery(id+"F0.wireOp",EDGE,"E117"),sQuery(id+"F0.wireOp",EDGE,"E118"),sQuery(id+"F0.wireOp",EDGE,"E119"),sQuery(id+"F0.wireOp",EDGE,"E120"),sQuery(id+"F0.wireOp",EDGE,"E121"),sQuery(id+"F0.wireOp",EDGE,"E122"),sQuery(id+"F0.wireOp",EDGE,"E123"),sQuery(id+"F0.wireOp",EDGE,"E124"),sQuery(id+"F0.wireOp",EDGE,"E125"),sQuery(id+"F0.wireOp",EDGE,"E126"),sQuery(id+"F0.wireOp",EDGE,"E127"),sQuery(id+"F0.wireOp",EDGE,"E128"),sQuery(id+"F0.wireOp",EDGE,"E129"),sQuery(id+"F0.wireOp",EDGE,"E130"),sQuery(id+"F0.wireOp",EDGE,"E131"),sQuery(id+"F0.wireOp",EDGE,"E132"),sQuery(id+"F0.wireOp",EDGE,"E133"),sQuery(id+"F0.wireOp",EDGE,"E134"),sQuery(id+"F0.wireOp",EDGE,"E135"),sQuery(id+"F0.wireOp",EDGE,"E136"),sQuery(id+"F0.wireOp",EDGE,"E137"),sQuery(id+"F0.wireOp",EDGE,"E138"),sQuery(id+"F0.wireOp",EDGE,"E139"),sQuery(id+"F0.wireOp",EDGE,"E140"),sQuery(id+"F0.wireOp",EDGE,"E141"),sQuery(id+"F0.wireOp",EDGE,"E142"),sQuery(id+"F0.wireOp",EDGE,"E143"),sQuery(id+"F0.wireOp",EDGE,"E144"),sQuery(id+"F0.wireOp",EDGE,"E145"),sQuery(id+"F0.wireOp",EDGE,"E146"),sQuery(id+"F0.wireOp",EDGE,"E147"),sQuery(id+"F0.wireOp",EDGE,"E148"),sQuery(id+"F0.wireOp",EDGE,"E149"),sQuery(id+"F0.wireOp",EDGE,"E150"),sQuery(id+"F0.wireOp",EDGE,"E151"),sQuery(id+"F0.wireOp",EDGE,"E152"),sQuery(id+"F0.wireOp",EDGE,"E153"),sQuery(id+"F0.wireOp",EDGE,"E154"),sQuery(id+"F0.wireOp",EDGE,"E155"),sQuery(id+"F0.wireOp",EDGE,"E156"),sQuery(id+"F0.wireOp",EDGE,"E157"),sQuery(id+"F0.wireOp",EDGE,"E158"),sQuery(id+"F0.wireOp",EDGE,"E159"),sQuery(id+"F0.wireOp",EDGE,"E160"),sQuery(id+"F0.wireOp",EDGE,"E161"),sQuery(id+"F0.wireOp",EDGE,"E162"),sQuery(id+"F0.wireOp",EDGE,"E163"),sQuery(id+"F0.wireOp",EDGE,"E164"),sQuery(id+"F0.wireOp",EDGE,"E165"),sQuery(id+"F0.wireOp",EDGE,"E166"),sQuery(id+"F0.wireOp",EDGE,"E167"),sQuery(id+"F0.wireOp",EDGE,"E168"),sQuery(id+"F0.wireOp",EDGE,"E169"),sQuery(id+"F0.wireOp",EDGE,"E170"),sQuery(id+"F0.wireOp",EDGE,"E171"),sQuery(id+"F0.wireOp",EDGE,"E172"),sQuery(id+"F0.wireOp",EDGE,"E173"),sQuery(id+"F0.wireOp",EDGE,"E174"),sQuery(id+"F0.wireOp",EDGE,"E175"),sQuery(id+"F0.wireOp",EDGE,"E176"),sQuery(id+"F0.wireOp",EDGE,"E177"),sQuery(id+"F0.wireOp",EDGE,"E178"),sQuery(id+"F0.wireOp",EDGE,"E179"),sQuery(id+"F0.wireOp",EDGE,"E180"),sQuery(id+"F0.wireOp",EDGE,"E181"),sQuery(id+"F0.wireOp",EDGE,"E182"),sQuery(id+"F0.wireOp",EDGE,"E183"),sQuery(id+"F0.wireOp",EDGE,"E184"),sQuery(id+"F0.wireOp",EDGE,"E185"),sQuery(id+"F0.wireOp",EDGE,"E186"),sQuery(id+"F0.wireOp",EDGE,"E187"),sQuery(id+"F0.wireOp",EDGE,"E188"),sQuery(id+"F0.wireOp",EDGE,"E189"),sQuery(id+"F0.wireOp",EDGE,"E190"),sQuery(id+"F0.wireOp",EDGE,"E191"),sQuery(id+"F0.wireOp",EDGE,"E192"),sQuery(id+"F0.wireOp",EDGE,"E193"),sQuery(id+"F0.wireOp",EDGE,"E194"),sQuery(id+"F0.wireOp",EDGE,"E195"),sQuery(id+"F0.wireOp",EDGE,"E196"),sQuery(id+"F0.wireOp",EDGE,"E197"),sQuery(id+"F0.wireOp",EDGE,"E198"),sQuery(id+"F0.wireOp",EDGE,"E199"),sQuery(id+"F0.wireOp",EDGE,"E200"),sQuery(id+"F0.wireOp",EDGE,"E201"),sQuery(id+"F0.wireOp",EDGE,"E202"),sQuery(id+"F0.wireOp",EDGE,"E203"),sQuery(id+"F0.wireOp",EDGE,"E204"),sQuery(id+"F0.wireOp",EDGE,"E205"),sQuery(id+"F0.wireOp",EDGE,"E206"),sQuery(id+"F0.wireOp",EDGE,"E207"),sQuery(id+"F0.wireOp",EDGE,"E208"),sQuery(id+"F0.wireOp",EDGE,"E209"),sQuery(id+"F0.wireOp",EDGE,"E210"),sQuery(id+"F0.wireOp",EDGE,"E211"),sQuery(id+"F0.wireOp",EDGE,"E212"),sQuery(id+"F0.wireOp",EDGE,"E213"),sQuery(id+"F0.wireOp",EDGE,"E214"),sQuery(id+"F0.wireOp",EDGE,"E215"),sQuery(id+"F0.wireOp",EDGE,"E216"),sQuery(id+"F0.wireOp",EDGE,"E217"),sQuery(id+"F0.wireOp",EDGE,"E218"),sQuery(id+"F0.wireOp",EDGE,"E219"),sQuery(id+"F0.wireOp",EDGE,"E220"),sQuery(id+"F0.wireOp",EDGE,"E221"),sQuery(id+"F0.wireOp",EDGE,"E222"),sQuery(id+"F0.wireOp",EDGE,"E223"),sQuery(id+"F0.wireOp",EDGE,"E224"),sQuery(id+"F0.wireOp",EDGE,"E225"),sQuery(id+"F0.wireOp",EDGE,"E226"),sQuery(id+"F0.wireOp",EDGE,"E227"),sQuery(id+"F0.wireOp",EDGE,"E228"),sQuery(id+"F0.wireOp",EDGE,"E229"),sQuery(id+"F0.wireOp",EDGE,"E230"),sQuery(id+"F0.wireOp",EDGE,"E231"),sQuery(id+"F0.wireOp",EDGE,"E232"),sQuery(id+"F0.wireOp",EDGE,"E233"),sQuery(id+"F0.wireOp",EDGE,"E234"),sQuery(id+"F0.wireOp",EDGE,"E235"),sQuery(id+"F0.wireOp",EDGE,"E236"),sQuery(id+"F0.wireOp",EDGE,"E237"),sQuery(id+"F0.wireOp",EDGE,"E238"),sQuery(id+"F0.wireOp",EDGE,"E239"),sQuery(id+"F0.wireOp",EDGE,"E240"),sQuery(id+"F0.wireOp",EDGE,"E241"),sQuery(id+"F0.wireOp",EDGE,"E242"),sQuery(id+"F0.wireOp",EDGE,"E243"),sQuery(id+"F0.wireOp",EDGE,"E244"),sQuery(id+"F0.wireOp",EDGE,"E245"),sQuery(id+"F0.wireOp",EDGE,"E246"),sQuery(id+"F0.wireOp",EDGE,"E247"),sQuery(id+"F0.wireOp",EDGE,"E248"),sQuery(id+"F0.wireOp",EDGE,"E249"),sQuery(id+"F0.wireOp",EDGE,"E250"),sQuery(id+"F0.wireOp",EDGE,"E251"),sQuery(id+"F0.wireOp",EDGE,"E252"),sQuery(id+"F0.wireOp",EDGE,"E253"),sQuery(id+"F0.wireOp",EDGE,"E254"),sQuery(id+"F0.wireOp",EDGE,"E255"),sQuery(id+"F0.wireOp",EDGE,"E256"),sQuery(id+"F0.wireOp",EDGE,"E257"),sQuery(id+"F0.wireOp",EDGE,"E258")])],"isStart":false});
            var sketch = newSketch(context, id + "F2", { "sketchPlane" : qUnion([Q0])});
            skText(sketch, "E259", { "text": "NAN", "fontName": "OpenSans-Bold.ttf"});
            const initialGuessF2  = {"E259": [-0.04355, 0.01904, 1, 0, 0.00848]};
            skSetInitialGuess(sketch, initialGuessF2);
            skSolve(sketch);
        }
        {
            var Q0;
            Q0 = qSketchRegion(id + "F2", true);
            extrude(context, id + "F3", {"entities" : qUnion([Q0]), "operationType" : NewBodyOperationType.ADD, "depth" : 1 * mm});
        }
        {
            var Q0;
            {var subQ0=sQuery(id+"F0.wireOp",EDGE,"E216");var subQ1=sQuery(id+"F0.wireOp",EDGE,"E215");var subQ2=sQuery(id+"F0.wireOp",EDGE,"E214");var subQ3=sQuery(id+"F0.wireOp",EDGE,"E213");var subQ4=sQuery(id+"F0.wireOp",EDGE,"E212");var subQ5=sQuery(id+"F0.wireOp",EDGE,"E211");var subQ6=sQuery(id+"F0.wireOp",EDGE,"E210");var subQ7=sQuery(id+"F0.wireOp",EDGE,"E209");var subQ8=sQuery(id+"F0.wireOp",EDGE,"E208");var subQ9=sQuery(id+"F0.wireOp",EDGE,"E207");var subQ10=sQuery(id+"F0.wireOp",EDGE,"E206");var subQ11=sQuery(id+"F0.wireOp",EDGE,"E205");var subQ12=sQuery(id+"F0.wireOp",EDGE,"E204");var subQ13=sQuery(id+"F0.wireOp",EDGE,"E203");var subQ14=sQuery(id+"F0.wireOp",EDGE,"E202");var subQ15=sQuery(id+"F0.wireOp",EDGE,"E201");var subQ16=sQuery(id+"F0.wireOp",EDGE,"E200");var subQ17=sQuery(id+"F0.wireOp",EDGE,"E199");var subQ18=sQuery(id+"F0.wireOp",EDGE,"E198");var subQ19=sQuery(id+"F0.wireOp",EDGE,"E197");var subQ20=sQuery(id+"F0.wireOp",EDGE,"E196");var subQ21=sQuery(id+"F0.wireOp",EDGE,"E195");var subQ22=sQuery(id+"F0.wireOp",EDGE,"E194");var subQ23=sQuery(id+"F0.wireOp",EDGE,"E193");var subQ24=sQuery(id+"F0.wireOp",EDGE,"E192");var subQ25=sQuery(id+"F0.wireOp",EDGE,"E191");var subQ26=sQuery(id+"F0.wireOp",EDGE,"E190");var subQ27=sQuery(id+"F0.wireOp",EDGE,"E189");var subQ28=sQuery(id+"F0.wireOp",EDGE,"E188");var subQ29=sQuery(id+"F0.wireOp",EDGE,"E187");var subQ30=sQuery(id+"F0.wireOp",EDGE,"E186");var subQ31=sQuery(id+"F0.wireOp",EDGE,"E185");var subQ32=sQuery(id+"F0.wireOp",EDGE,"E184");var subQ33=sQuery(id+"F0.wireOp",EDGE,"E183");var subQ34=sQuery(id+"F0.wireOp",EDGE,"E182");var subQ35=sQuery(id+"F0.wireOp",EDGE,"E181");var subQ36=sQuery(id+"F0.wireOp",EDGE,"E180");var subQ37=sQuery(id+"F0.wireOp",EDGE,"E179");var subQ38=sQuery(id+"F0.wireOp",EDGE,"E178");var subQ39=sQuery(id+"F0.wireOp",EDGE,"E177");var subQ40=sQuery(id+"F0.wireOp",EDGE,"E176");var subQ41=sQuery(id+"F0.wireOp",EDGE,"E175");var subQ42=sQuery(id+"F0.wireOp",EDGE,"E174");var subQ43=sQuery(id+"F0.wireOp",EDGE,"E173");var subQ44=sQuery(id+"F0.wireOp",EDGE,"E172");var subQ45=sQuery(id+"F0.wireOp",EDGE,"E171");var subQ46=sQuery(id+"F0.wireOp",EDGE,"E170");var subQ47=sQuery(id+"F0.wireOp",EDGE,"E169");var subQ48=sQuery(id+"F0.wireOp",EDGE,"E168");var subQ49=sQuery(id+"F0.wireOp",EDGE,"E167");var subQ50=sQuery(id+"F0.wireOp",EDGE,"E166");var subQ51=sQuery(id+"F0.wireOp",EDGE,"E165");var subQ52=sQuery(id+"F0.wireOp",EDGE,"E164");var subQ53=sQuery(id+"F0.wireOp",EDGE,"E163");var subQ54=sQuery(id+"F0.wireOp",EDGE,"E162");var subQ55=sQuery(id+"F0.wireOp",EDGE,"E161");var subQ56=sQuery(id+"F0.wireOp",EDGE,"E160");var subQ57=sQuery(id+"F0.wireOp",EDGE,"E159");var subQ58=sQuery(id+"F0.wireOp",EDGE,"E158");var subQ59=sQuery(id+"F0.wireOp",EDGE,"E157");var subQ60=sQuery(id+"F0.wireOp",EDGE,"E156");var subQ61=sQuery(id+"F0.wireOp",EDGE,"E155");var subQ62=sQuery(id+"F0.wireOp",EDGE,"E154");var subQ63=sQuery(id+"F0.wireOp",EDGE,"E153");var subQ64=sQuery(id+"F0.wireOp",EDGE,"E152");var subQ65=sQuery(id+"F0.wireOp",EDGE,"E151");var subQ66=sQuery(id+"F0.wireOp",EDGE,"E150");var subQ67=sQuery(id+"F0.wireOp",EDGE,"E149");var subQ68=sQuery(id+"F0.wireOp",EDGE,"E148");var subQ69=sQuery(id+"F0.wireOp",EDGE,"E147");var subQ70=sQuery(id+"F0.wireOp",EDGE,"E146");var subQ71=sQuery(id+"F0.wireOp",EDGE,"E145");var subQ72=sQuery(id+"F0.wireOp",EDGE,"E144");var subQ73=sQuery(id+"F0.wireOp",EDGE,"E143");var subQ74=sQuery(id+"F0.wireOp",EDGE,"E142");var subQ75=sQuery(id+"F0.wireOp",EDGE,"E141");var subQ76=sQuery(id+"F0.wireOp",EDGE,"E140");var subQ77=sQuery(id+"F0.wireOp",EDGE,"E139");var subQ78=sQuery(id+"F0.wireOp",EDGE,"E138");var subQ79=sQuery(id+"F0.wireOp",EDGE,"E137");var subQ80=sQuery(id+"F0.wireOp",EDGE,"E136");var subQ81=sQuery(id+"F0.wireOp",EDGE,"E135");var subQ82=sQuery(id+"F0.wireOp",EDGE,"E134");var subQ83=sQuery(id+"F0.wireOp",EDGE,"E133");var subQ84=sQuery(id+"F0.wireOp",EDGE,"E132");var subQ85=sQuery(id+"F0.wireOp",EDGE,"E131");var subQ86=sQuery(id+"F0.wireOp",EDGE,"E130");var subQ87=sQuery(id+"F0.wireOp",EDGE,"E129");var subQ88=sQuery(id+"F0.wireOp",EDGE,"E128");var subQ89=sQuery(id+"F0.wireOp",EDGE,"E127");var subQ90=sQuery(id+"F0.wireOp",EDGE,"E126");var subQ91=sQuery(id+"F0.wireOp",EDGE,"E125");var subQ92=sQuery(id+"F0.wireOp",EDGE,"E124");var subQ93=sQuery(id+"F0.wireOp",EDGE,"E123");var subQ94=sQuery(id+"F0.wireOp",EDGE,"E122");var subQ95=sQuery(id+"F0.wireOp",EDGE,"E121");var subQ96=sQuery(id+"F0.wireOp",EDGE,"E120");var subQ97=sQuery(id+"F0.wireOp",EDGE,"E119");var subQ98=sQuery(id+"F0.wireOp",EDGE,"E118");var subQ99=sQuery(id+"F0.wireOp",EDGE,"E117");var subQ100=sQuery(id+"F0.wireOp",EDGE,"E116");var subQ101=sQuery(id+"F0.wireOp",EDGE,"E115");var subQ102=sQuery(id+"F0.wireOp",EDGE,"E114");var subQ103=sQuery(id+"F0.wireOp",EDGE,"E113");var subQ104=sQuery(id+"F0.wireOp",EDGE,"E112");var subQ105=sQuery(id+"F0.wireOp",EDGE,"E111");var subQ106=sQuery(id+"F0.wireOp",EDGE,"E110");var subQ107=sQuery(id+"F0.wireOp",EDGE,"E109");var subQ108=sQuery(id+"F0.wireOp",EDGE,"E108");var subQ109=sQuery(id+"F0.wireOp",EDGE,"E46");var subQ110=sQuery(id+"F0.wireOp",EDGE,"E45");var subQ111=sQuery(id+"F0.wireOp",EDGE,"E44");var subQ112=sQuery(id+"F0.wireOp",EDGE,"E43");var subQ113=sQuery(id+"F0.wireOp",EDGE,"E42");var subQ114=sQuery(id+"F0.wireOp",EDGE,"E41");var subQ115=sQuery(id+"F0.wireOp",EDGE,"E40");var subQ116=sQuery(id+"F0.wireOp",EDGE,"E39");var subQ117=sQuery(id+"F0.wireOp",EDGE,"E38");var subQ118=sQuery(id+"F0.wireOp",EDGE,"E37");var subQ119=sQuery(id+"F0.wireOp",EDGE,"E36");var subQ120=sQuery(id+"F0.wireOp",EDGE,"E35");var subQ121=sQuery(id+"F0.wireOp",EDGE,"E34");var subQ122=sQuery(id+"F0.wireOp",EDGE,"E33");var subQ123=sQuery(id+"F0.wireOp",EDGE,"E32");var subQ124=sQuery(id+"F0.wireOp",EDGE,"E31");var subQ125=sQuery(id+"F0.wireOp",EDGE,"E30");var subQ126=sQuery(id+"F0.wireOp",EDGE,"E29");var subQ127=sQuery(id+"F0.wireOp",EDGE,"E28");var subQ128=sQuery(id+"F0.wireOp",EDGE,"E27");var subQ129=sQuery(id+"F0.wireOp",EDGE,"E26");var subQ130=sQuery(id+"F0.wireOp",EDGE,"E25");var subQ131=sQuery(id+"F0.wireOp",EDGE,"E24");var subQ132=sQuery(id+"F0.wireOp",EDGE,"E23");var subQ133=sQuery(id+"F0.wireOp",EDGE,"E22");var subQ134=sQuery(id+"F0.wireOp",EDGE,"E8");var subQ135=sQuery(id+"F0.wireOp",EDGE,"E7");var subQ136=sQuery(id+"F0.wireOp",EDGE,"E6");var subQ137=sQuery(id+"F0.wireOp",EDGE,"E5");var subQ138=sQuery(id+"F0.wireOp",EDGE,"E4");var subQ139=sQuery(id+"F0.wireOp",EDGE,"E9");var subQ140=sQuery(id+"F0.wireOp",EDGE,"E47");var subQ141=sQuery(id+"F0.wireOp",EDGE,"E217");var subQ142=sQuery(id+"F0.wireOp",EDGE,"E0");var subQ143=sQuery(id+"F0.wireOp",EDGE,"E107");var subQ144=sQuery(id+"F0.wireOp",EDGE,"E21");var subQ145=sQuery(id+"F0.wireOp",EDGE,"E3");var subQ146=sQuery(id+"F0.wireOp",EDGE,"E1");var subQ147=sQuery(id+"F0.wireOp",EDGE,"E2");var subQ148=sQuery(id+"F0.wireOp",EDGE,"E10");var subQ149=sQuery(id+"F0.wireOp",EDGE,"E11");var subQ150=sQuery(id+"F0.wireOp",EDGE,"E12");var subQ151=sQuery(id+"F0.wireOp",EDGE,"E13");var subQ152=sQuery(id+"F0.wireOp",EDGE,"E14");var subQ153=sQuery(id+"F0.wireOp",EDGE,"E15");var subQ154=sQuery(id+"F0.wireOp",EDGE,"E16");var subQ155=sQuery(id+"F0.wireOp",EDGE,"E17");var subQ156=sQuery(id+"F0.wireOp",EDGE,"E18");var subQ157=sQuery(id+"F0.wireOp",EDGE,"E19");var subQ158=sQuery(id+"F0.wireOp",EDGE,"E20");var subQ159=sQuery(id+"F0.wireOp",EDGE,"E48");var subQ160=sQuery(id+"F0.wireOp",EDGE,"E49");var subQ161=sQuery(id+"F0.wireOp",EDGE,"E50");var subQ162=sQuery(id+"F0.wireOp",EDGE,"E51");var subQ163=sQuery(id+"F0.wireOp",EDGE,"E52");var subQ164=sQuery(id+"F0.wireOp",EDGE,"E53");var subQ165=sQuery(id+"F0.wireOp",EDGE,"E55");var subQ166=sQuery(id+"F0.wireOp",EDGE,"E54");var subQ167=sQuery(id+"F0.wireOp",EDGE,"E57");var subQ168=sQuery(id+"F0.wireOp",EDGE,"E56");var subQ169=sQuery(id+"F0.wireOp",EDGE,"E58");var subQ170=sQuery(id+"F0.wireOp",EDGE,"E59");var subQ171=sQuery(id+"F0.wireOp",EDGE,"E60");var subQ172=sQuery(id+"F0.wireOp",EDGE,"E61");var subQ173=sQuery(id+"F0.wireOp",EDGE,"E62");var subQ174=sQuery(id+"F0.wireOp",EDGE,"E63");var subQ175=sQuery(id+"F0.wireOp",EDGE,"E64");var subQ176=sQuery(id+"F0.wireOp",EDGE,"E66");var subQ177=sQuery(id+"F0.wireOp",EDGE,"E65");var subQ178=sQuery(id+"F0.wireOp",EDGE,"E67");var subQ179=sQuery(id+"F0.wireOp",EDGE,"E70");var subQ180=sQuery(id+"F0.wireOp",EDGE,"E69");var subQ181=sQuery(id+"F0.wireOp",EDGE,"E68");var subQ182=sQuery(id+"F0.wireOp",EDGE,"E71");var subQ183=sQuery(id+"F0.wireOp",EDGE,"E72");var subQ184=sQuery(id+"F0.wireOp",EDGE,"E75");var subQ185=sQuery(id+"F0.wireOp",EDGE,"E74");var subQ186=sQuery(id+"F0.wireOp",EDGE,"E73");var subQ187=sQuery(id+"F0.wireOp",EDGE,"E76");var subQ188=sQuery(id+"F0.wireOp",EDGE,"E77");var subQ189=sQuery(id+"F0.wireOp",EDGE,"E78");var subQ190=sQuery(id+"F0.wireOp",EDGE,"E79");var subQ191=sQuery(id+"F0.wireOp",EDGE,"E80");var subQ192=sQuery(id+"F0.wireOp",EDGE,"E82");var subQ193=sQuery(id+"F0.wireOp",EDGE,"E81");var subQ194=sQuery(id+"F0.wireOp",EDGE,"E83");var subQ195=sQuery(id+"F0.wireOp",EDGE,"E85");var subQ196=sQuery(id+"F0.wireOp",EDGE,"E84");var subQ197=sQuery(id+"F0.wireOp",EDGE,"E86");var subQ198=sQuery(id+"F0.wireOp",EDGE,"E87");var subQ199=sQuery(id+"F0.wireOp",EDGE,"E88");var subQ200=sQuery(id+"F0.wireOp",EDGE,"E89");var subQ201=sQuery(id+"F0.wireOp",EDGE,"E90");var subQ202=sQuery(id+"F0.wireOp",EDGE,"E91");var subQ203=sQuery(id+"F0.wireOp",EDGE,"E93");var subQ204=sQuery(id+"F0.wireOp",EDGE,"E92");var subQ205=sQuery(id+"F0.wireOp",EDGE,"E94");var subQ206=sQuery(id+"F0.wireOp",EDGE,"E95");var subQ207=sQuery(id+"F0.wireOp",EDGE,"E96");var subQ208=sQuery(id+"F0.wireOp",EDGE,"E97");var subQ209=sQuery(id+"F0.wireOp",EDGE,"E98");var subQ210=sQuery(id+"F0.wireOp",EDGE,"E99");var subQ211=sQuery(id+"F0.wireOp",EDGE,"E100");var subQ212=sQuery(id+"F0.wireOp",EDGE,"E101");var subQ213=sQuery(id+"F0.wireOp",EDGE,"E102");var subQ214=sQuery(id+"F0.wireOp",EDGE,"E103");var subQ215=sQuery(id+"F0.wireOp",EDGE,"E104");var subQ216=sQuery(id+"F0.wireOp",EDGE,"E105");var subQ217=sQuery(id+"F0.wireOp",EDGE,"E106");var subQ218=sQuery(id+"F0.wireOp",EDGE,"E218");var subQ219=sQuery(id+"F0.wireOp",EDGE,"E219");var subQ220=sQuery(id+"F0.wireOp",EDGE,"E220");var subQ221=sQuery(id+"F0.wireOp",EDGE,"E222");var subQ222=sQuery(id+"F0.wireOp",EDGE,"E221");var subQ223=sQuery(id+"F0.wireOp",EDGE,"E223");var subQ224=sQuery(id+"F0.wireOp",EDGE,"E224");var subQ225=sQuery(id+"F0.wireOp",EDGE,"E225");var subQ226=sQuery(id+"F0.wireOp",EDGE,"E226");var subQ227=sQuery(id+"F0.wireOp",EDGE,"E227");var subQ228=sQuery(id+"F0.wireOp",EDGE,"E228");var subQ229=sQuery(id+"F0.wireOp",EDGE,"E230");var subQ230=sQuery(id+"F0.wireOp",EDGE,"E229");var subQ231=sQuery(id+"F0.wireOp",EDGE,"E231");var subQ232=sQuery(id+"F0.wireOp",EDGE,"E232");var subQ233=sQuery(id+"F0.wireOp",EDGE,"E233");var subQ234=sQuery(id+"F0.wireOp",EDGE,"E234");var subQ235=sQuery(id+"F0.wireOp",EDGE,"E236");var subQ236=sQuery(id+"F0.wireOp",EDGE,"E235");var subQ237=sQuery(id+"F0.wireOp",EDGE,"E237");var subQ238=sQuery(id+"F0.wireOp",EDGE,"E238");var subQ239=sQuery(id+"F0.wireOp",EDGE,"E240");var subQ240=sQuery(id+"F0.wireOp",EDGE,"E239");var subQ241=sQuery(id+"F0.wireOp",EDGE,"E241");var subQ242=sQuery(id+"F0.wireOp",EDGE,"E242");var subQ243=sQuery(id+"F0.wireOp",EDGE,"E243");var subQ244=sQuery(id+"F0.wireOp",EDGE,"E244");var subQ245=sQuery(id+"F0.wireOp",EDGE,"E245");var subQ246=sQuery(id+"F0.wireOp",EDGE,"E246");var subQ247=sQuery(id+"F0.wireOp",EDGE,"E247");var subQ248=sQuery(id+"F0.wireOp",EDGE,"E248");var subQ249=sQuery(id+"F0.wireOp",EDGE,"E249");var subQ250=sQuery(id+"F0.wireOp",EDGE,"E250");var subQ251=sQuery(id+"F0.wireOp",EDGE,"E251");var subQ252=sQuery(id+"F0.wireOp",EDGE,"E252");var subQ253=sQuery(id+"F0.wireOp",EDGE,"E253");var subQ254=sQuery(id+"F0.wireOp",EDGE,"E254");var subQ255=sQuery(id+"F0.wireOp",EDGE,"E255");var subQ256=sQuery(id+"F0.wireOp",EDGE,"E256");var subQ257=sQuery(id+"F0.wireOp",EDGE,"E257");var subQ258=sQuery(id+"F0.wireOp",EDGE,"E258");Q0=makeQuery(id+"F3.boolean.opBoolean","SPLIT",FACE,{"disambiguationData":[TD([makeQuery(id+"F1.opExtrude","SWEPT_FACE",FACE,{"disambiguationData":[OSD([subQ142])]})])],"derivedFrom":makeQuery(id+"F1.opExtrude","CAP_FACE",FACE,{"disambiguationData":[OSD([subQ142,subQ146,subQ147,subQ145,subQ138,subQ137,subQ136,subQ135,subQ134,subQ139,subQ148,subQ149,subQ150,subQ151,subQ152,subQ153,subQ154,subQ155,subQ156,subQ157,subQ158,subQ144,subQ133,subQ132,subQ131,subQ130,subQ129,subQ128,subQ127,subQ126,subQ125,subQ124,subQ123,subQ122,subQ121,subQ120,subQ119,subQ118,subQ117,subQ116,subQ115,subQ114,subQ113,subQ112,subQ111,subQ110,subQ109,subQ140,subQ159,subQ160,subQ161,subQ162,subQ163,subQ164,subQ166,subQ165,subQ168,subQ167,subQ169,subQ170,subQ171,subQ172,subQ173,subQ174,subQ175,subQ177,subQ176,subQ178,subQ181,subQ180,subQ179,subQ182,subQ183,subQ186,subQ185,subQ184,subQ187,subQ188,subQ189,subQ190,subQ191,subQ193,subQ192,subQ194,subQ196,subQ195,subQ197,subQ198,subQ199,subQ200,subQ201,subQ202,subQ204,subQ203,subQ205,subQ206,subQ207,subQ208,subQ209,subQ210,subQ211,subQ212,subQ213,subQ214,subQ215,subQ216,subQ217,subQ143,subQ108,subQ107,subQ106,subQ105,subQ104,subQ103,subQ102,subQ101,subQ100,subQ99,subQ98,subQ97,subQ96,subQ95,subQ94,subQ93,subQ92,subQ91,subQ90,subQ89,subQ88,subQ87,subQ86,subQ85,subQ84,subQ83,subQ82,subQ81,subQ80,subQ79,subQ78,subQ77,subQ76,subQ75,subQ74,subQ73,subQ72,subQ71,subQ70,subQ69,subQ68,subQ67,subQ66,subQ65,subQ64,subQ63,subQ62,subQ61,subQ60,subQ59,subQ58,subQ57,subQ56,subQ55,subQ54,subQ53,subQ52,subQ51,subQ50,subQ49,subQ48,subQ47,subQ46,subQ45,subQ44,subQ43,subQ42,subQ41,subQ40,subQ39,subQ38,subQ37,subQ36,subQ35,subQ34,subQ33,subQ32,subQ31,subQ30,subQ29,subQ28,subQ27,subQ26,subQ25,subQ24,subQ23,subQ22,subQ21,subQ20,subQ19,subQ18,subQ17,subQ16,subQ15,subQ14,subQ13,subQ12,subQ11,subQ10,subQ9,subQ8,subQ7,subQ6,subQ5,subQ4,subQ3,subQ2,subQ1,subQ0,subQ141,subQ218,subQ219,subQ220,subQ222,subQ221,subQ223,subQ224,subQ225,subQ226,subQ227,subQ228,subQ230,subQ229,subQ231,subQ232,subQ233,subQ234,subQ236,subQ235,subQ237,subQ238,subQ240,subQ239,subQ241,subQ242,subQ243,subQ244,subQ245,subQ246,subQ247,subQ248,subQ249,subQ250,subQ251,subQ252,subQ253,subQ254,subQ255,subQ256,subQ257,subQ258])],"isStart":false})});}
            var sketch = newSketch(context, id + "F4", { "sketchPlane" : qUnion([Q0])});
            skCircle(sketch, "E260", {"center": v(-10.22, 40.8) * mm, "radius": 2.75 * mm});
            skSolve(sketch);
        }
        {
            var Q0;
            Q0 = qSketchRegion(id + "F4", true);
            extrude(context, id + "F5", {"entities" : qUnion([Q0]), "operationType" : NewBodyOperationType.REMOVE, "oppositeDirection" : true, "depth" : 25 * mm});
        }
    });
